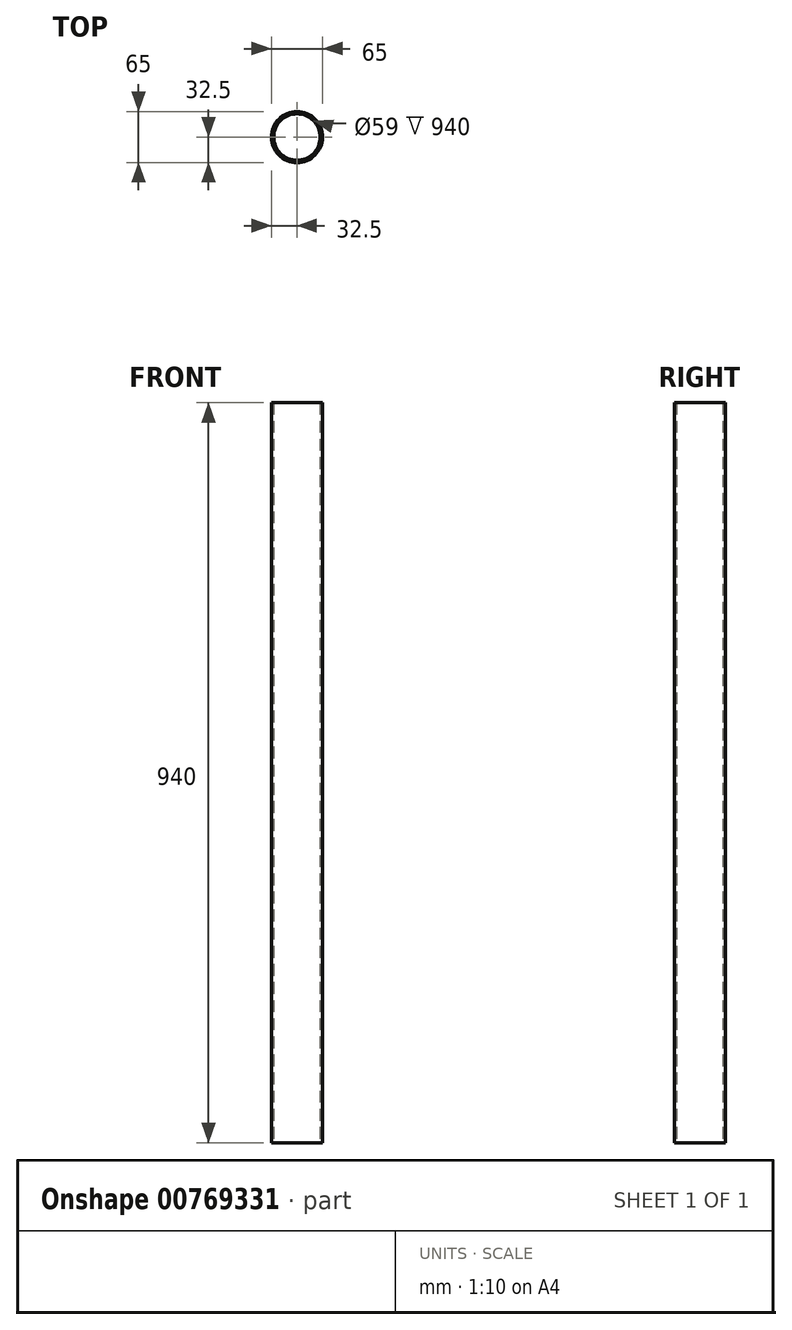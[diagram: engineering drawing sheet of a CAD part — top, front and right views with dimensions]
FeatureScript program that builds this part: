
annotation { "Feature Type Name" : "Feature", "Feature Type Description" : "" }
export const myFeature = defineFeature(function(context is Context, id is Id, definition is map)
    precondition{}
    {
        {
            var Q0;
            Q0=qCreatedBy(makeId("Top.planeOp"),FACE);
            var sketch = newSketch(context, id + "F0", { "sketchPlane" : qUnion([Q0])});
            skCircle(sketch, "E0", {"center": v(0, 0) * mm, "radius": 29.5 * mm});
            skCircle(sketch, "E1", {"center": v(0, 0) * mm, "radius": 32.5 * mm});
            skSolve(sketch);
        }
        {
            var Q0;
            Q0=makeQuery(id+"F0.imprint","IMPRINT",FACE,{"disambiguationData":[TD([[makeQuery(id+"F0.imprint","IMPRINT",EDGE,{"derivedFrom":sQuery(id+"F0.wireOp",EDGE,"E0")}),-1.0]])]});
            extrude(context, id + "F1", {"entities" : qUnion([Q0]), "depth" : (1000 - 60) * mm, "offsetDistance" : 25 * mm});
        }
    });
